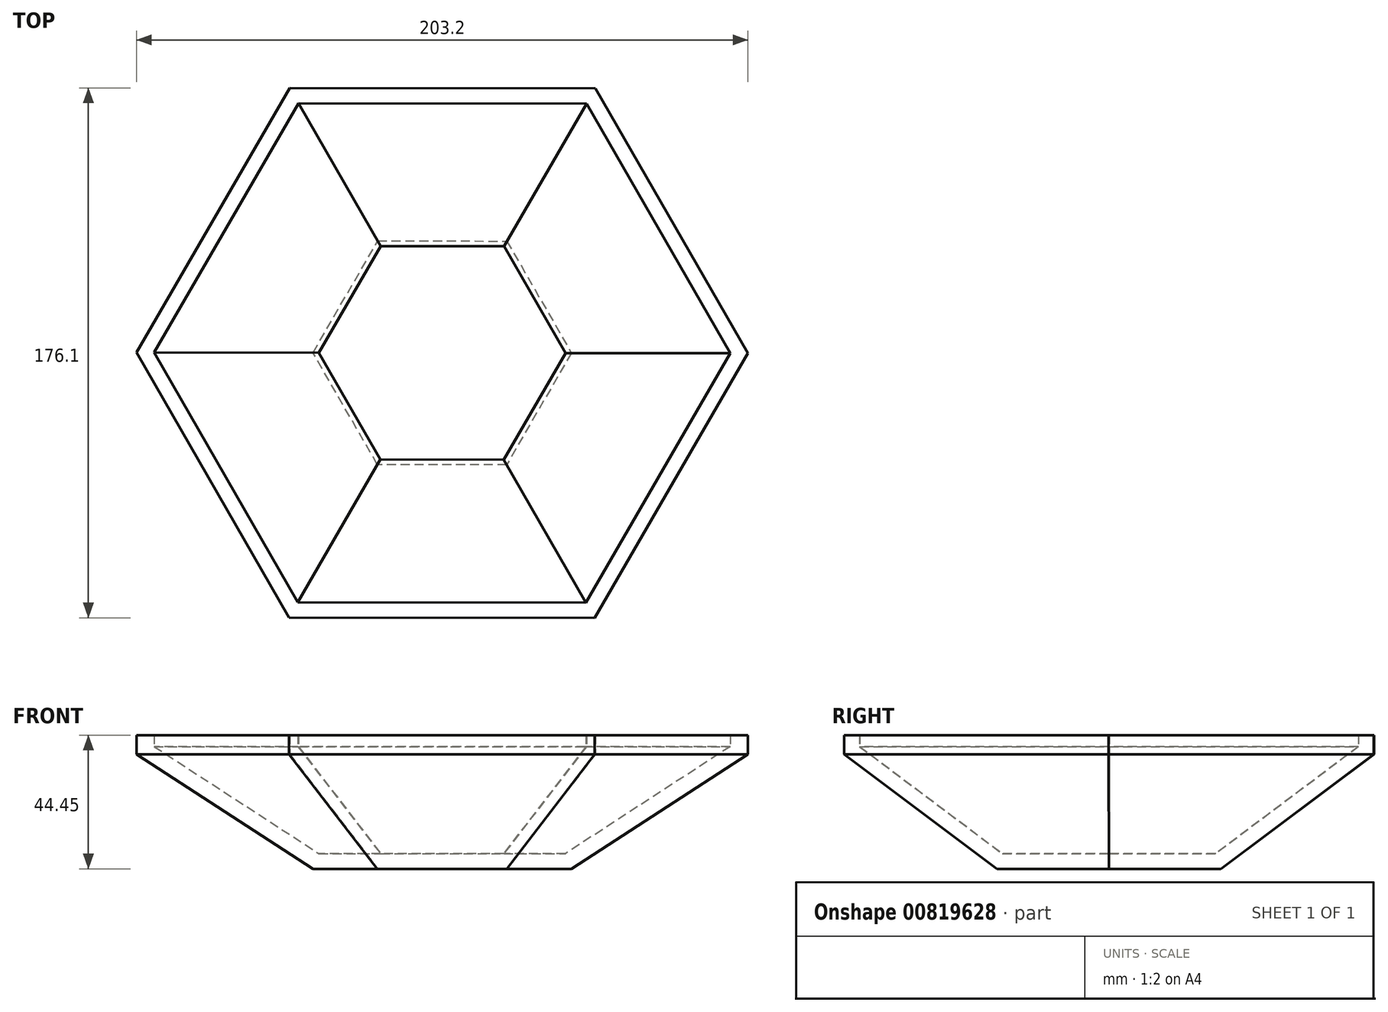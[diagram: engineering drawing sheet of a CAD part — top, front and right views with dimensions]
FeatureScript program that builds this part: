
annotation { "Feature Type Name" : "Feature", "Feature Type Description" : "" }
export const myFeature = defineFeature(function(context is Context, id is Id, definition is map)
    precondition{}
    {
        {
            var Q0;
            Q0=qCreatedBy(makeId("Top.planeOp"),FACE);
            var sketch = newSketch(context, id + "F0", { "sketchPlane" : qUnion([Q0])});
            skCircle(sketch, "E0.cCircle", {"center": v(0, 0) * mm, "radius": 87.99 * mm, "construction": true});
            skLineSegment(sketch, "E0.0", {"start": v(101.6, -0.13) * mm, "end": v(50.69, -88.05) * mm});
            skLineSegment(sketch, "E0.1", {"start": v(50.69, -88.05) * mm, "end": v(-50.91, -87.92) * mm});
            skLineSegment(sketch, "E0.2", {"start": v(-50.91, -87.92) * mm, "end": v(-101.6, 0.13) * mm});
            skLineSegment(sketch, "E0.3", {"start": v(-101.6, 0.13) * mm, "end": v(-50.69, 88.05) * mm});
            skLineSegment(sketch, "E0.4", {"start": v(-50.69, 88.05) * mm, "end": v(50.91, 87.92) * mm});
            skLineSegment(sketch, "E0.5", {"start": v(50.91, 87.92) * mm, "end": v(101.6, -0.13) * mm});
            skPoint(sketch, "E0.0.midPoint", {"position": v(76.14, -44.1) * mm});
            skSolve(sketch);
        }
        {
            var Q0;
            Q0=qCreatedBy(makeId("Top.planeOp"),FACE);
            cPlane(context, id + "F1", {"entities" : qUnion([Q0]), "cplaneType" : CPlaneType.OFFSET, "offset" : 38.1 * mm, "oppositeDirection" : true, "width" : 152.4 * mm, "height" : 152.4 * mm});
        }
        {
            var Q0;
            Q0=qCreatedBy(id+"F1.planeOp",FACE);
            var sketch = newSketch(context, id + "F2", { "sketchPlane" : qUnion([Q0])});
            skLineSegment(sketch, "E1.0", {"start": v(101.6, -0.13) * mm, "end": v(50.69, -88.05) * mm, "construction": true});
            skLineSegment(sketch, "E1.1", {"start": v(50.69, -88.05) * mm, "end": v(-50.91, -87.92) * mm, "construction": true});
            skLineSegment(sketch, "E1.2", {"start": v(-50.91, -87.92) * mm, "end": v(-101.6, 0.13) * mm, "construction": true});
            skLineSegment(sketch, "E1.3", {"start": v(-101.6, 0.13) * mm, "end": v(-50.69, 88.05) * mm, "construction": true});
            skLineSegment(sketch, "E1.4", {"start": v(-50.69, 88.05) * mm, "end": v(50.91, 87.92) * mm, "construction": true});
            skLineSegment(sketch, "E1.5", {"start": v(50.91, 87.92) * mm, "end": v(101.6, -0.13) * mm, "construction": true});
            skCircle(sketch, "E1.6", {"center": v(0, 0) * mm, "radius": 87.99 * mm, "construction": true});
            skLineSegment(sketch, "E2.0", {"start": v(-42.94, 0.06) * mm, "end": v(-21.42, 37.22) * mm});
            skLineSegment(sketch, "E2.1", {"start": v(21.52, 37.16) * mm, "end": v(42.94, -0.06) * mm});
            skLineSegment(sketch, "E2.2", {"start": v(42.94, -0.06) * mm, "end": v(21.42, -37.22) * mm});
            skLineSegment(sketch, "E2.3", {"start": v(-21.42, 37.22) * mm, "end": v(21.52, 37.16) * mm});
            skLineSegment(sketch, "E2.4", {"start": v(21.42, -37.22) * mm, "end": v(-21.52, -37.16) * mm});
            skLineSegment(sketch, "E2.5", {"start": v(-21.52, -37.16) * mm, "end": v(-42.94, 0.06) * mm});
            skSolve(sketch);
        }
        {
            var Q0;
            Q0=makeQuery(id+"F0.imprint","IMPRINT",FACE,{"disambiguationData":[TD([[makeQuery(id+"F0.imprint","IMPRINT",EDGE,{"derivedFrom":sQuery(id+"F0.wireOp",EDGE,"E0.0")}),-1.0]])]});
            var Q1;
            Q1=makeQuery(id+"F2.imprint","IMPRINT",FACE,{"disambiguationData":[TD([[makeQuery(id+"F2.imprint","IMPRINT",EDGE,{"derivedFrom":sQuery(id+"F2.wireOp",EDGE,"E2.0")}),-1.0]])]});
            loft(context, id + "F3", {"sheetProfilesArray" : [{ "sheetProfileEntities" : qUnion([Q0]) }, { "sheetProfileEntities" : qUnion([Q1]) }]});
        }
        {
            var Q0;
            Q0=makeQuery(id+"F0.imprint","IMPRINT",FACE,{"disambiguationData":[TD([[makeQuery(id+"F0.imprint","IMPRINT",EDGE,{"derivedFrom":sQuery(id+"F0.wireOp",EDGE,"E0.0")}),-1.0]])]});
            extrude(context, id + "F4", {"entities" : qUnion([Q0]), "operationType" : NewBodyOperationType.ADD, "depth" : 6.35 * mm, "offsetDistance" : 25.4 * mm});
        }
        {
            var Q0;
            Q0=makeQuery(id+"F4.opExtrude","CAP_FACE",FACE,{"disambiguationData":[OSD([sQuery(id+"F0.wireOp",EDGE,"E0.0"),sQuery(id+"F0.wireOp",EDGE,"E0.1"),sQuery(id+"F0.wireOp",EDGE,"E0.2"),sQuery(id+"F0.wireOp",EDGE,"E0.3"),sQuery(id+"F0.wireOp",EDGE,"E0.4"),sQuery(id+"F0.wireOp",EDGE,"E0.5")])],"isStart":false});
            shell(context, id + "F5", {"entities" : qUnion([Q0]), "thickness" : 5.08 * mm});
        }
    });
